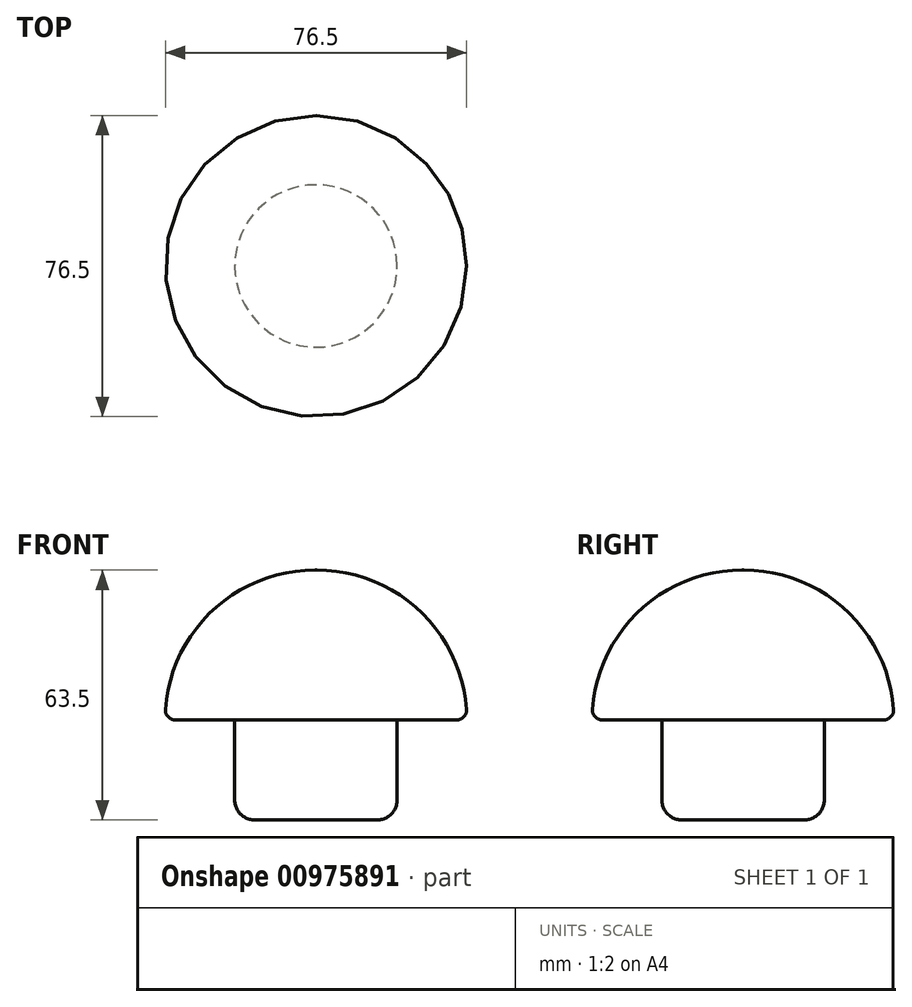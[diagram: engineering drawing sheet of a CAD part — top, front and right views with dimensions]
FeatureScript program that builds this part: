
annotation { "Feature Type Name" : "Feature", "Feature Type Description" : "" }
export const myFeature = defineFeature(function(context is Context, id is Id, definition is map)
    precondition{}
    {
        {
            var Q0;
            Q0=qCreatedBy(makeId("Top.planeOp"),FACE);
            var sketch = newSketch(context, id + "F0", { "sketchPlane" : qUnion([Q0])});
            skCircle(sketch, "E0", {"center": v(0, 0) * mm, "radius": 20.63 * mm});
            skSolve(sketch);
        }
        {
            var Q0;
            Q0=makeQuery(id+"F0.imprint","IMPRINT",FACE,{"disambiguationData":[TD([[makeQuery(id+"F0.imprint","IMPRINT",EDGE,{"derivedFrom":sQuery(id+"F0.wireOp",EDGE,"E0")}),1.0]])]});
            extrude(context, id + "F1", {"entities" : qUnion([Q0]), "depth" : 25.4 * mm, "offsetDistance" : 25.4 * mm});
        }
        {
            var Q0;
            Q0=qCreatedBy(makeId("Top.planeOp"),FACE);
            cPlane(context, id + "F2", {"entities" : qUnion([Q0]), "cplaneType" : CPlaneType.OFFSET, "offset" : 25.4 * mm, "width" : 152.4 * mm, "height" : 152.4 * mm});
        }
        {
            var Q0;
            Q0=qCreatedBy(id+"F2.planeOp",FACE);
            var sketch = newSketch(context, id + "F3", { "sketchPlane" : qUnion([Q0])});
            skCircle(sketch, "E1", {"center": v(0, 0) * mm, "radius": 38.34 * mm});
            skSolve(sketch);
        }
        {
            var Q0;
            Q0 = qSketchRegion(id + "F3", true);
            extrude(context, id + "F4", {"entities" : qUnion([Q0]), "depth" : 38.1 * mm, "offsetDistance" : 25.4 * mm});
        }
        {
            var Q0;
            Q0=makeQuery(id+"F4.opExtrude","CAP_FACE",FACE,{"disambiguationData":[OSD([sQuery(id+"F3.wireOp",EDGE,"E1")])],"isStart":false});
            fillet(context, id + "F5", {"entities" : qUnion([Q0]), "radius" : 38.1 * mm, "tangentPropagation" : true, "allowEdgeOverflow" : false});
        }
        {
            var Q0;
            Q0=makeQuery(id+"F1.opExtrude","CAP_FACE",FACE,{"disambiguationData":[OSD([sQuery(id+"F0.wireOp",EDGE,"E0")])],"isStart":true});
            fillet(context, id + "F6", {"entities" : qUnion([Q0]), "radius" : 5.08 * mm, "tangentPropagation" : true, "allowEdgeOverflow" : false});
        }
        {
            var Q0;
            {var subQ0=sQuery(id+"F3.wireOp",EDGE,"E1");Q0=makeQuery(id+"F5.opFillet","BLEND_EDGE",EDGE,{"blendedFrom":[makeQuery(id+"F4.opExtrude","CAP_EDGE",EDGE,{"disambiguationData":[OSD([subQ0])],"isStart":false}),makeQuery(id+"F4.opExtrude","CAP_FACE",FACE,{"disambiguationData":[OSD([subQ0])],"isStart":true})],"blendedInto":[makeQuery(id+"F4.opExtrude","CAP_FACE",FACE,{"disambiguationData":[OSD([subQ0])],"isStart":true})]});}
            fillet(context, id + "F7", {"entities" : qUnion([Q0]), "radius" : 2.54 * mm, "tangentPropagation" : true, "allowEdgeOverflow" : false});
        }
    });
